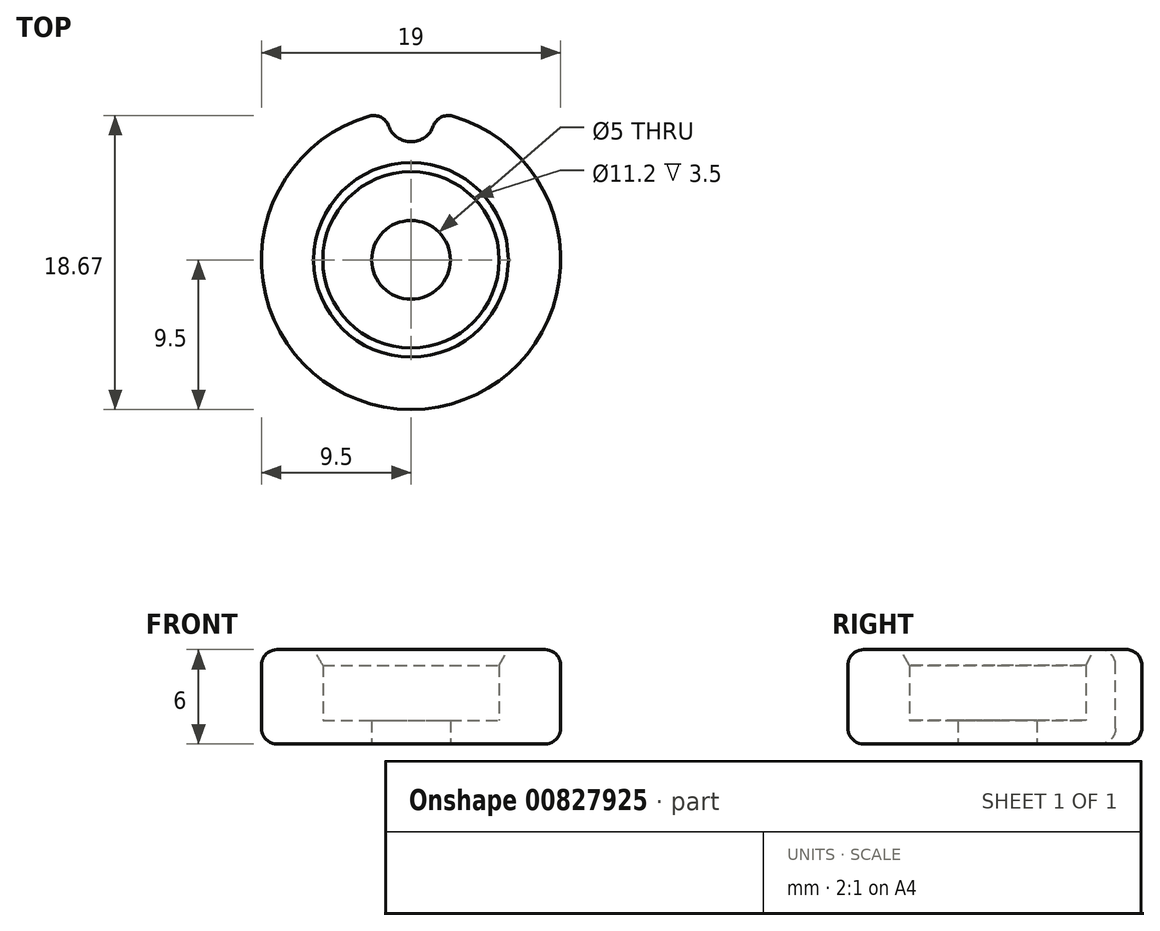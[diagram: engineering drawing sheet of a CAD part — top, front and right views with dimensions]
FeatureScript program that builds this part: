
annotation { "Feature Type Name" : "Feature", "Feature Type Description" : "" }
export const myFeature = defineFeature(function(context is Context, id is Id, definition is map)
    precondition{}
    {
        {
            var Q0;
            Q0=qCreatedBy(makeId("Front.planeOp"),FACE);
            var sketch = newSketch(context, id + "F0", { "sketchPlane" : qUnion([Q0])});
            skLineSegment(sketch, "E0", {"start": v(0, 0) * mm, "end": v(0, 5.46) * mm, "construction": true});
            skLineSegment(sketch, "E1", {"start": v(-2.5, 0) * mm, "end": v(-2.5, 1.5) * mm});
            skLineSegment(sketch, "E2", {"start": v(-2.5, 1.5) * mm, "end": v(-5.6, 1.5) * mm});
            skLineSegment(sketch, "E3", {"start": v(-5.6, 1.5) * mm, "end": v(-5.6, 6) * mm});
            skLineSegment(sketch, "E4", {"start": v(-5.6, 6) * mm, "end": v(-9.5, 6) * mm});
            skLineSegment(sketch, "E5", {"start": v(-9.5, 6) * mm, "end": v(-9.5, 0) * mm});
            skLineSegment(sketch, "E6", {"start": v(-9.5, 0) * mm, "end": v(-2.5, 0) * mm});
            skSolve(sketch);
        }
        {
            var Q0;
            Q0=qSketchRegion(id+"F0",true);
            var Q1;
            Q1=sQuery(id+"F0.wireOp",EDGE,"E0");
            revolve(context, id + "F1", {"surfaceOperationType" : NewSurfaceOperationType.NEW, "entities" : qUnion([Q0]), "axis" : qUnion([Q1]), "revolveType" : RevolveType.FULL});
        }
        {
            var Q0;
            Q0=makeQuery(id+"F1.opRevolve","SWEPT_EDGE",EDGE,{"disambiguationData":[OSD([sQuery(id+"F0.wireOp",EDGE,"E5"),sQuery(id+"F0.wireOp",EDGE,"E6")])]});
            var Q1;
            Q1=makeQuery(id+"F1.opRevolve","SWEPT_EDGE",EDGE,{"disambiguationData":[OSD([sQuery(id+"F0.wireOp",EDGE,"E4"),sQuery(id+"F0.wireOp",EDGE,"E5")])]});
            fillet(context, id + "F2", {"entities" : qUnion([Q0, Q1]), "radius" : 1 * mm, "tangentPropagation" : true, "allowEdgeOverflow" : false});
        }
        {
            var Q0;
            Q0=makeQuery(id+"F1.opRevolve","SWEPT_EDGE",EDGE,{"disambiguationData":[OSD([sQuery(id+"F0.wireOp",EDGE,"E3"),sQuery(id+"F0.wireOp",EDGE,"E4")])]});
            chamfer(context, id + "F3", {"entities" : qUnion([Q0]), "chamferType" : ChamferType.OFFSET_ANGLE, "width" : 1 * mm, "oppositeDirection" : true, "angle" : 30 * degree, "tangentPropagation" : true});
        }
        {
            var Q0;
            Q0=makeQuery(id+"F1.opRevolve","SWEPT_FACE",FACE,{"disambiguationData":[OSD([sQuery(id+"F0.wireOp",EDGE,"E4")])]});
            var sketch = newSketch(context, id + "F4", { "sketchPlane" : qUnion([Q0])});
            skLineSegment(sketch, "E7.bottom", {"start": v(-1.5, 12.4) * mm, "end": v(1.5, 12.4) * mm});
            skLineSegment(sketch, "E7.top", {"start": v(-1.5, 9) * mm, "end": v(1.5, 9) * mm, "construction": true});
            skLineSegment(sketch, "E7.left", {"start": v(-1.5, 12.4) * mm, "end": v(-1.5, 9) * mm});
            skLineSegment(sketch, "E7.right", {"start": v(1.5, 12.4) * mm, "end": v(1.5, 9) * mm});
            skArc(sketch, "E8", {"start": v(-1.5, 9) * mm, "mid": v(0, 7.5) * mm, "end": v(1.5, 9) * mm});
            skSolve(sketch);
        }
        {
            var Q0;
            Q0=qSketchRegion(id+"F4",true);
            var Q1;
            Q1=makeQuery(id+"F1.opRevolve","SWEPT_FACE",FACE,{"disambiguationData":[OSD([sQuery(id+"F0.wireOp",EDGE,"E6")])]});
            extrude(context, id + "F5", {"entities" : qUnion([Q0]), "operationType" : NewBodyOperationType.REMOVE, "endBound" : BoundingType.UP_TO_SURFACE, "oppositeDirection" : true, "depth" : 25 * mm, "endBoundEntityFace" : qUnion([Q1]), "offsetDistance" : 25 * mm});
        }
        {
            var Q0;
            Q0=makeQuery(id+"F5.boolean.opBoolean","INTERSECT",EDGE,{"derivedFrom":[makeQuery(id+"F1.opRevolve","SWEPT_FACE",FACE,{"disambiguationData":[OSD([sQuery(id+"F0.wireOp",EDGE,"E5")])]}),makeQuery(id+"F5.opExtrude","SWEPT_FACE",FACE,{"disambiguationData":[OSD([sQuery(id+"F4.wireOp",EDGE,"E7.right")])]})]});
            var Q1;
            Q1=makeQuery(id+"F5.boolean.opBoolean","INTERSECT",EDGE,{"derivedFrom":[makeQuery(id+"F1.opRevolve","SWEPT_FACE",FACE,{"disambiguationData":[OSD([sQuery(id+"F0.wireOp",EDGE,"E5")])]}),makeQuery(id+"F5.opExtrude","SWEPT_FACE",FACE,{"disambiguationData":[OSD([sQuery(id+"F4.wireOp",EDGE,"E7.left")])]})]});
            fillet(context, id + "F6", {"entities" : qUnion([Q0, Q1]), "radius" : 1 * mm, "tangentPropagation" : true, "allowEdgeOverflow" : false});
        }
    });
